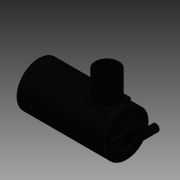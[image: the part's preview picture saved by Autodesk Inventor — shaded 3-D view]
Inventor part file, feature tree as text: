
AUTODESK INVENTOR PART (.ipt)
format: ipt  version: 2013 (Build 170138000, 138)  size: 178,176 bytes
history: native  units: in
note: dims shown in document units (in); Inventor stores cm internally (conversion verified against a paired STEP export)
features: extrude x7, sketch x6, plane x5, fillet x2, revolve x1, projected_geometry x1
ambient origin geometry x8: Origin, YZ Plane, XZ Plane, XY Plane, X Axis, Y Axis, Z Axis, Center Point
feature tree (22):
  revolve  "Revolution1"  [1 undecoded]
  plane  "Work Plane3"
  extrude  "Extrusion3"  TaperAngle=0.0deg  [1 undecoded]
  plane  "Work Plane4"
  extrude  "Extrusion4"  TaperAngle=0.0deg  [1 undecoded]
  plane  "Work Plane5"
  extrude  "Extrusion5"  Depth=0.5906in
  plane  "Work Plane6"
  sketch  "Sketch8"  dims[d79=0.1575in d80=0.0in d85=0.1575in d86=0.0in]
  extrude  "Extrusion6"  Depth=0.1575in TaperAngle=0.0deg
  extrude  "Extrusion8"  Depth=0.0394in
  extrude  "Extrusion9"  Depth=0.0394in
  fillet  "Fillet2"  [1 undecoded]
  fillet  "Fillet3"  Radius=0.7874in
  plane  "Work Plane7"
  extrude  "Extrusion11"  [1 undecoded]
  sketch  "Sketch4"  dims[d30=90.0deg d31=0.0in]
  sketch  "Sketch5"  dims[d46=0.0787in d47=0.0in d48=0.0in]
  sketch  "Sketch6"  dims[d64=0.0787in d65=0.0in d68=0.0in]
  sketch  "Sketch7"  dims[d69=0.0787in d70=0.0in d71=0.5906in]
  projected_geometry  "Projected Loop1"
  sketch  "Sketch9"  dims[d87=0.7087in d88=0.0in d89=0.0394in d90=0.0394in d91=-0.5906in d96=0.7874in d97=0.0in]
note: 5 required parameter values undecoded (feature->parameter linkage not recoverable at this tier; creation-order binding heuristic only, values carry confidence <= 0.55)